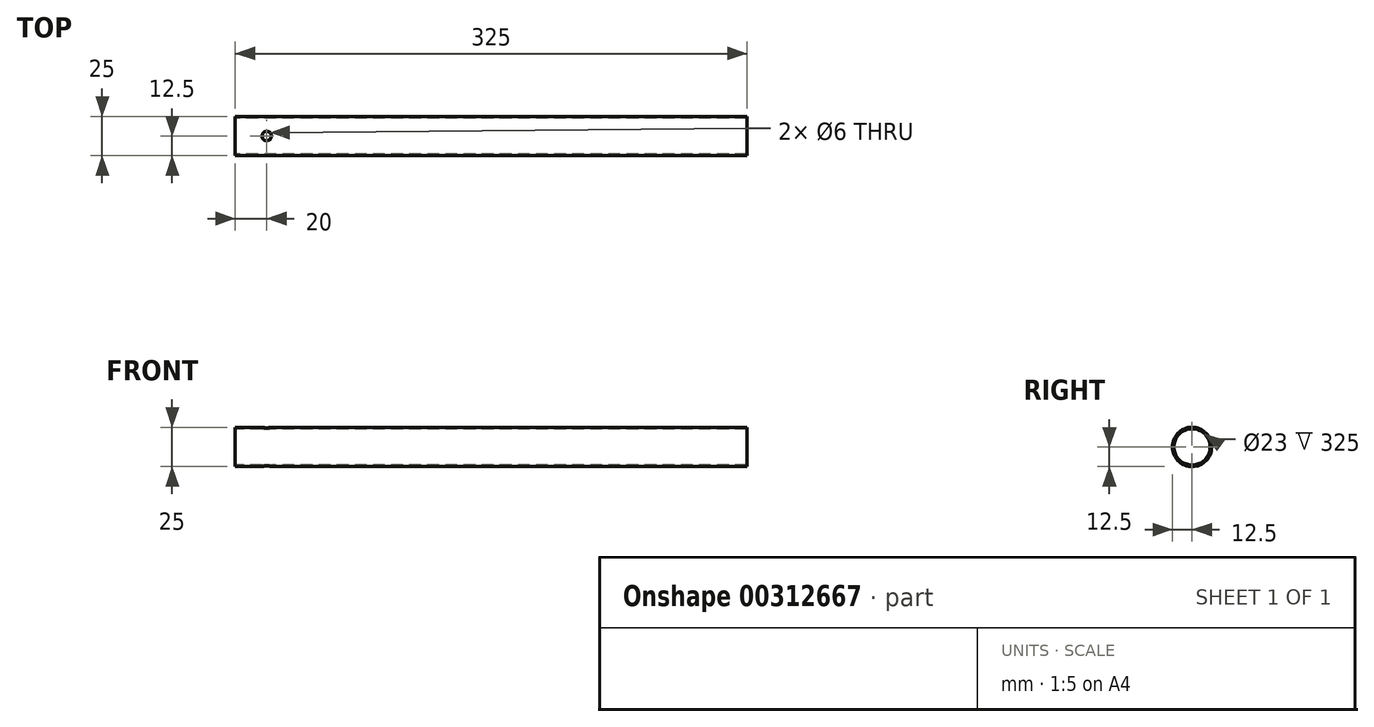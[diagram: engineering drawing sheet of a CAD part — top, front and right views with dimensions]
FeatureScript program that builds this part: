
annotation { "Feature Type Name" : "Feature", "Feature Type Description" : "" }
export const myFeature = defineFeature(function(context is Context, id is Id, definition is map)
    precondition{}
    {
        {
            var Q0;
            Q0=qCreatedBy(makeId("Right.planeOp"),FACE);
            var sketch = newSketch(context, id + "F0", { "sketchPlane" : qUnion([Q0])});
            skCircle(sketch, "E0", {"center": v(0, 0) * mm, "radius": 11.5 * mm});
            skCircle(sketch, "E1", {"center": v(0, 0) * mm, "radius": 12.5 * mm});
            skSolve(sketch);
        }
        {
            var Q0;
            Q0=makeQuery(id+"F0.imprint","IMPRINT",FACE,{"disambiguationData":[TD([[makeQuery(id+"F0.imprint","IMPRINT",EDGE,{"derivedFrom":sQuery(id+"F0.wireOp",EDGE,"E0")}),-1.0]])]});
            extrude(context, id + "F1", {"entities" : qUnion([Q0]), "depth" : 325 * mm});
        }
        {
            var Q0;
            Q0=qCreatedBy(makeId("Top.planeOp"),FACE);
            var sketch = newSketch(context, id + "F2", { "sketchPlane" : qUnion([Q0])});
            skLineSegment(sketch, "E2", {"start": v(0, 0) * mm, "end": v(20, 0) * mm});
            skSolve(sketch);
        }
        {
            var Q0;
            Q0=sQuery(id+"F2.wireOp",VERTEX,"E2.end");
            var Q1;
            Q1=makeQuery(id+"F1.opExtrude","SWEPT_BODY",BODY,{"disambiguationData":[OSD([sQuery(id+"F0.wireOp",EDGE,"E0"),sQuery(id+"F0.wireOp",EDGE,"E1")])]});
            hole(context, id + "F3", {"style" : HoleStyle.SIMPLE, "endStyle" : HoleEndStyle.THROUGH, "oppositeDirection" : true, "holeDiameter" : 6 * mm, "tappedDepth" : 12 * mm, "tapClearance" : 3, "locations" : qUnion([Q0]), "scope" : qUnion([Q1])});
        }
        {
            var Q0;
            Q0=sQuery(id+"F2.wireOp",VERTEX,"E2.end");
            var Q1;
            Q1=makeQuery(id+"F1.opExtrude","SWEPT_BODY",BODY,{"disambiguationData":[OSD([sQuery(id+"F0.wireOp",EDGE,"E0"),sQuery(id+"F0.wireOp",EDGE,"E1")])]});
            hole(context, id + "F4", {"style" : HoleStyle.SIMPLE, "endStyle" : HoleEndStyle.THROUGH, "holeDiameter" : 6 * mm, "tappedDepth" : 12 * mm, "tapClearance" : 3, "locations" : qUnion([Q0]), "scope" : qUnion([Q1])});
        }
    });
